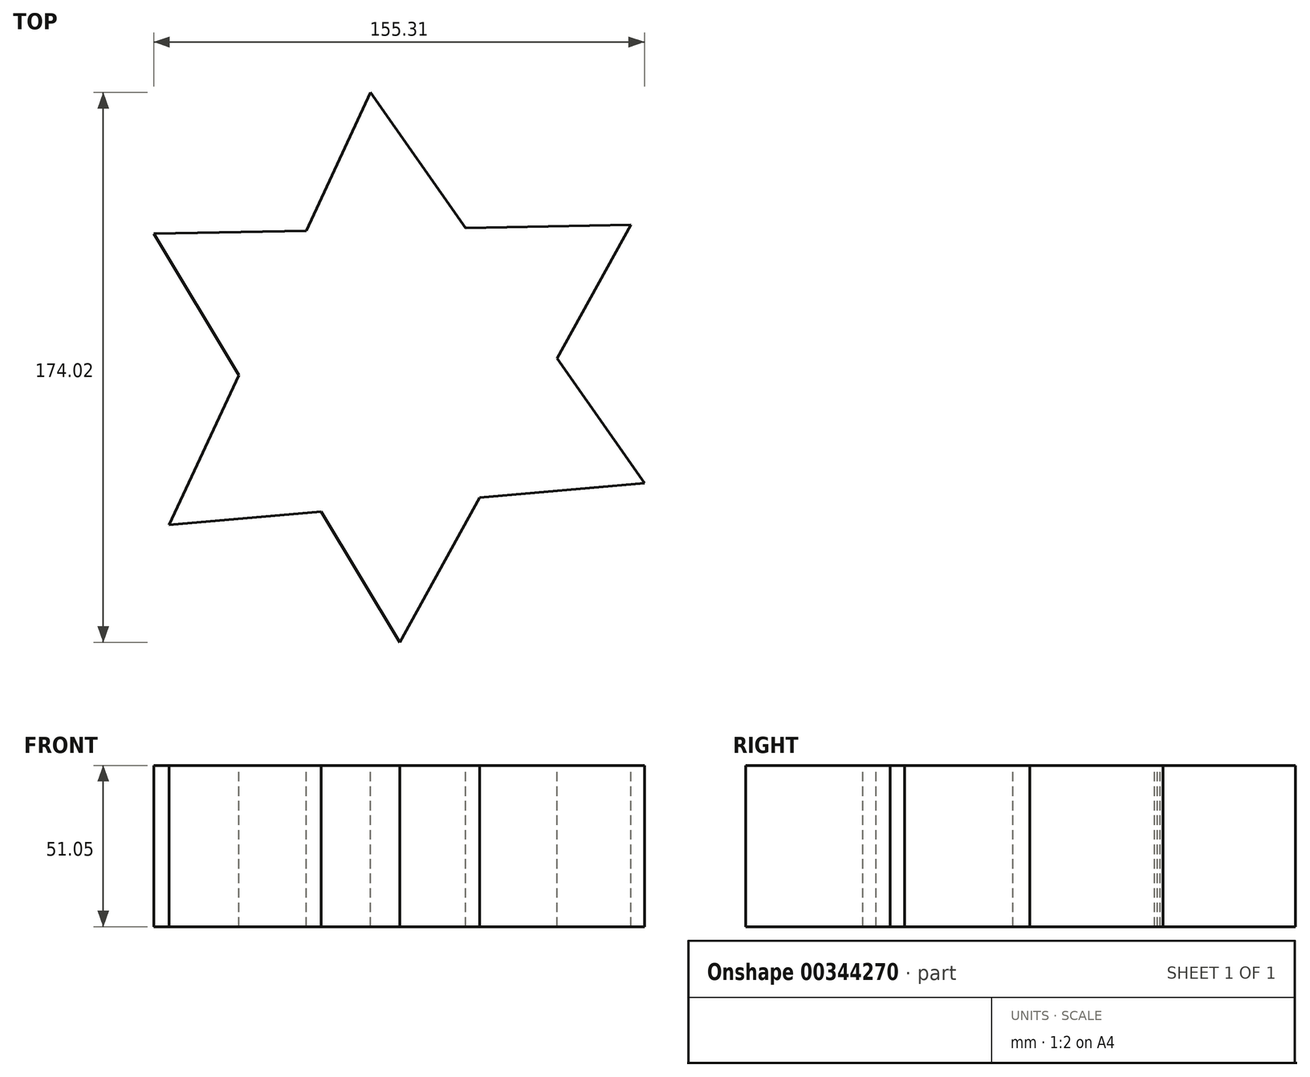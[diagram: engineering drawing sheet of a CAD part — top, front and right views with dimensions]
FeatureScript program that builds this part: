
annotation { "Feature Type Name" : "Feature", "Feature Type Description" : "" }
export const myFeature = defineFeature(function(context is Context, id is Id, definition is map)
    precondition{}
    {
        {
            var Q0;
            Q0=qCreatedBy(makeId("Top.planeOp"),FACE);
            var sketch = newSketch(context, id + "F0", { "sketchPlane" : qUnion([Q0])});
            skLineSegment(sketch, "E0.0", {"start": v(79.04, -36.8) * mm, "end": v(26.91, -41.4) * mm});
            skLineSegment(sketch, "E0.1", {"start": v(-71.39, -50.06) * mm, "end": v(-49.3, -2.61) * mm});
            skLineSegment(sketch, "E0.2", {"start": v(-7.66, 86.85) * mm, "end": v(22.39, 44) * mm});
            skLineSegment(sketch, "E1.0", {"start": v(74.72, 44.94) * mm, "end": v(51.34, 2.72) * mm});
            skLineSegment(sketch, "E1.1", {"start": v(1.56, -87.17) * mm, "end": v(-23.31, -45.82) * mm});
            skLineSegment(sketch, "E1.2", {"start": v(-76.27, 42.24) * mm, "end": v(-28.02, 43.1) * mm});
            skLineSegment(sketch, "E2.trimOffspring", {"start": v(-28.02, 43.1) * mm, "end": v(-7.66, 86.85) * mm});
            skLineSegment(sketch, "E3.trimOffspring", {"start": v(22.39, 44) * mm, "end": v(74.72, 44.94) * mm});
            skLineSegment(sketch, "E4.trimOffspring", {"start": v(51.34, 2.72) * mm, "end": v(79.04, -36.8) * mm});
            skLineSegment(sketch, "E5.trimOffspring", {"start": v(26.91, -41.4) * mm, "end": v(1.56, -87.17) * mm});
            skLineSegment(sketch, "E6.trimOffspring", {"start": v(-23.31, -45.82) * mm, "end": v(-71.39, -50.06) * mm});
            skLineSegment(sketch, "E7.trimOffspring", {"start": v(-49.3, -2.61) * mm, "end": v(-76.27, 42.24) * mm});
            skSolve(sketch);
        }
        {
            var Q0;
            Q0 = qSketchRegion(id + "F0", true);
            extrude(context, id + "F1", {"entities" : qUnion([Q0]), "oppositeDirection" : true, "depth" : 51.05 * mm});
        }
    });
